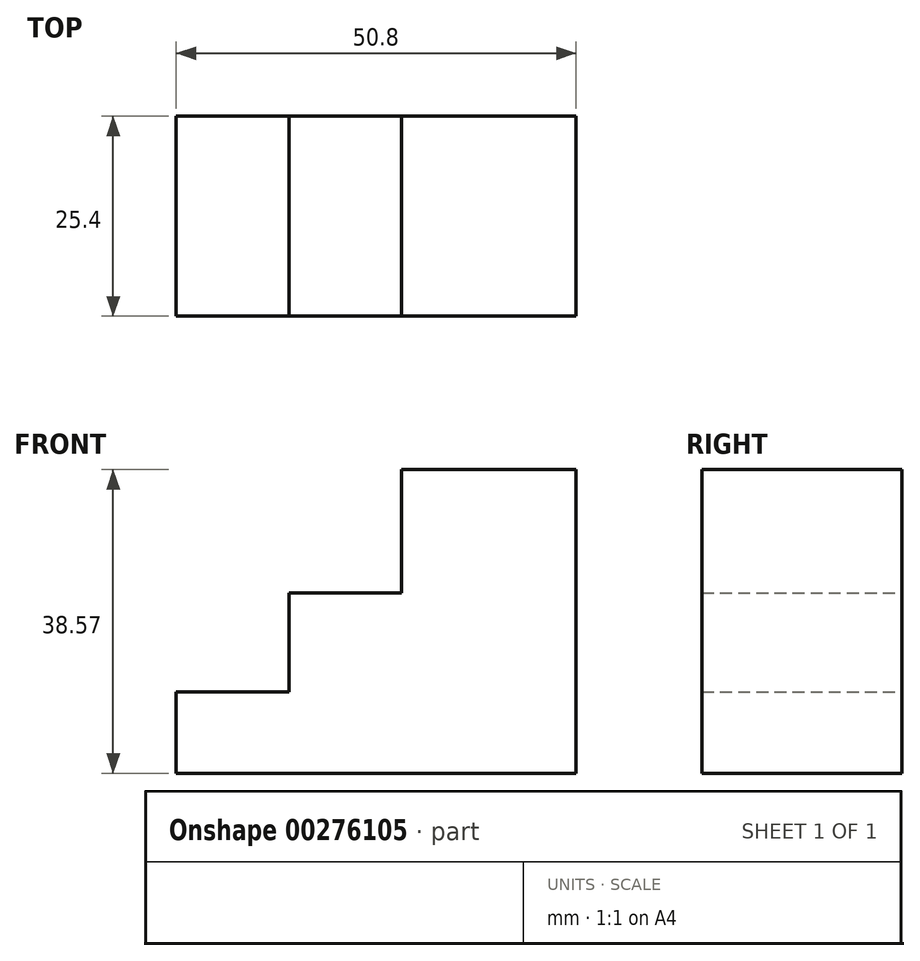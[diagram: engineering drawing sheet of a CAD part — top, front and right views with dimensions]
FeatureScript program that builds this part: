
annotation { "Feature Type Name" : "Feature", "Feature Type Description" : "" }
export const myFeature = defineFeature(function(context is Context, id is Id, definition is map)
    precondition{}
    {
        {
            var Q0;
            Q0=qCreatedBy(makeId("Front.planeOp"),FACE);
            var sketch = newSketch(context, id + "F0", { "sketchPlane" : qUnion([Q0])});
            skLineSegment(sketch, "E0", {"start": v(0, 0) * mm, "end": v(-50.8, 0) * mm});
            skLineSegment(sketch, "E1", {"start": v(-50.8, 0) * mm, "end": v(-50.8, 10.31) * mm});
            skLineSegment(sketch, "E2", {"start": v(-50.8, 10.31) * mm, "end": v(-36.47, 10.31) * mm});
            skLineSegment(sketch, "E3", {"start": v(-36.47, 10.31) * mm, "end": v(-36.47, 22.91) * mm});
            skLineSegment(sketch, "E4", {"start": v(-36.47, 22.91) * mm, "end": v(-22.15, 22.91) * mm});
            skLineSegment(sketch, "E5", {"start": v(-22.15, 22.91) * mm, "end": v(-22.15, 38.57) * mm});
            skLineSegment(sketch, "E6", {"start": v(-22.15, 38.57) * mm, "end": v(0, 38.57) * mm});
            skLineSegment(sketch, "E7", {"start": v(0, 38.57) * mm, "end": v(0, 0) * mm});
            skSolve(sketch);
        }
        {
            var Q0;
            Q0=makeQuery(id+"F0.imprint","IMPRINT",FACE,{"disambiguationData":[TD([[makeQuery(id+"F0.imprint","IMPRINT",EDGE,{"derivedFrom":sQuery(id+"F0.wireOp",EDGE,"E0")}),-1.0]])]});
            extrude(context, id + "F1", {"entities" : qUnion([Q0]), "depth" : 25.4 * mm});
        }
    });
